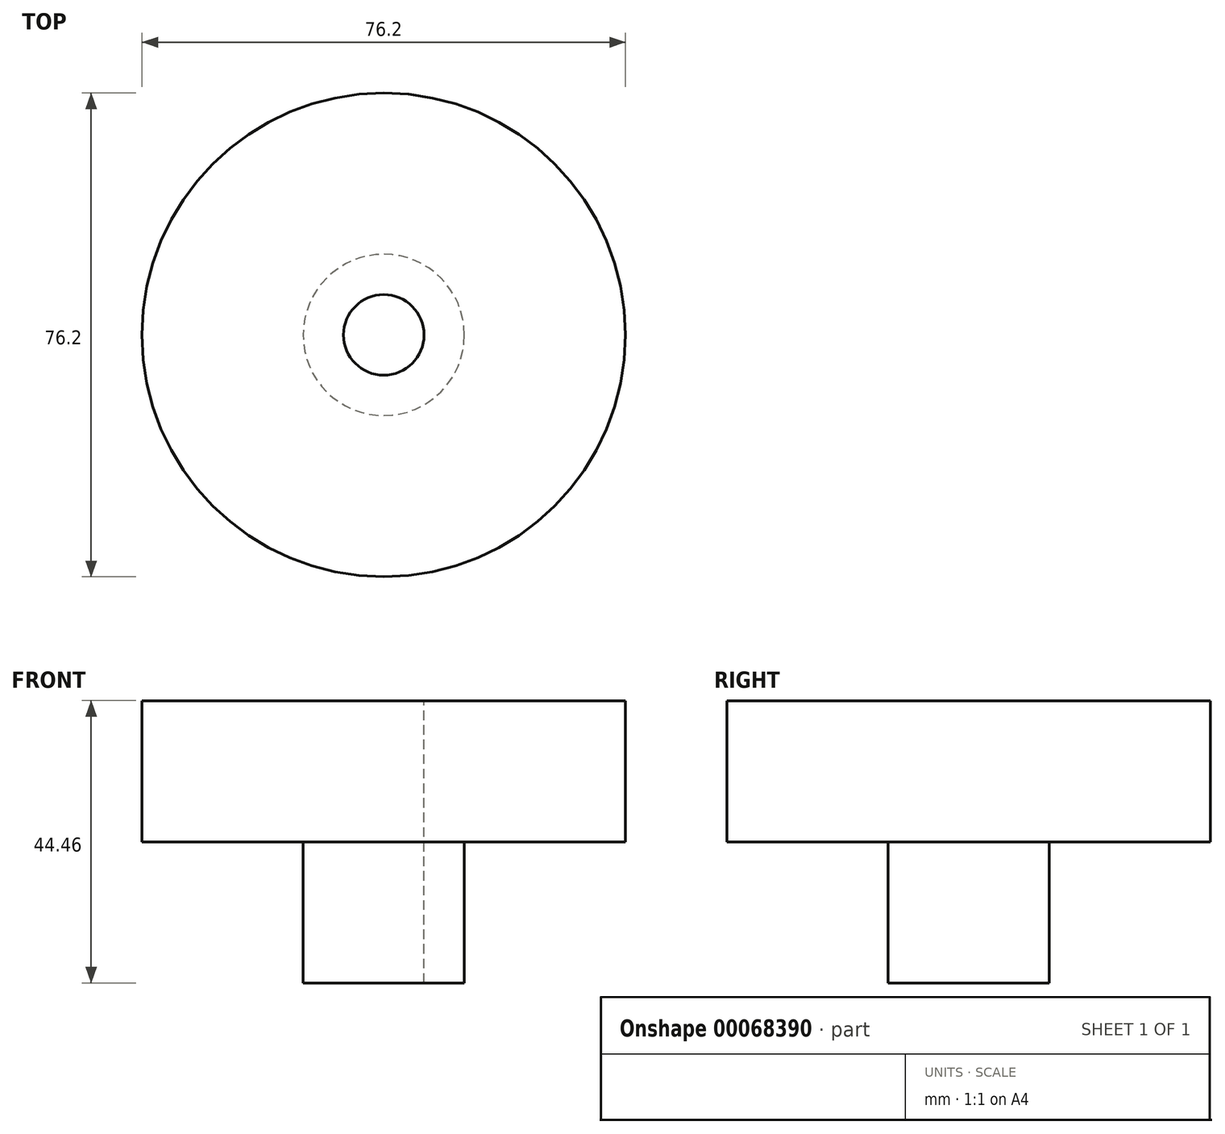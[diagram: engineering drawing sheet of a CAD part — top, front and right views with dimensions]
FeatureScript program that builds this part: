
annotation { "Feature Type Name" : "Feature", "Feature Type Description" : "" }
export const myFeature = defineFeature(function(context is Context, id is Id, definition is map)
    precondition{}
    {
        {
            var Q0;
            Q0=qCreatedBy(makeId("Top.planeOp"),FACE);
            var sketch = newSketch(context, id + "F0", { "sketchPlane" : qUnion([Q0])});
            skCircle(sketch, "E0", {"center": v(0, 0) * mm, "radius": 38.1 * mm});
            skSolve(sketch);
        }
        {
            var Q0;
            Q0=makeQuery(id+"F0.imprint","IMPRINT",FACE,{"disambiguationData":[TD([[makeQuery(id+"F0.imprint","IMPRINT",EDGE,{"derivedFrom":sQuery(id+"F0.wireOp",EDGE,"E0")}),1.0]])]});
            extrude(context, id + "F1", {"entities" : qUnion([Q0]), "depth" : 22.22 * mm});
        }
        {
            var Q0;
            Q0=makeQuery(id+"F1.opExtrude","CAP_FACE",FACE,{"disambiguationData":[OSD([sQuery(id+"F0.wireOp",EDGE,"E0")])],"isStart":false});
            var sketch = newSketch(context, id + "F2", { "sketchPlane" : qUnion([Q0])});
            skCircle(sketch, "E1", {"center": v(0, 0) * mm, "radius": 6.35 * mm});
            skSolve(sketch);
        }
        {
            var Q0;
            Q0=makeQuery(id+"F2.imprint","IMPRINT",FACE,{"disambiguationData":[TD([[makeQuery(id+"F2.imprint","IMPRINT",EDGE,{"derivedFrom":sQuery(id+"F2.wireOp",EDGE,"E1")}),1.0]])]});
            extrude(context, id + "F3", {"entities" : qUnion([Q0]), "operationType" : NewBodyOperationType.REMOVE, "oppositeDirection" : true, "depth" : 35.5 * mm});
        }
        {
            var Q0;
            Q0=makeQuery(id+"F1.opExtrude","CAP_FACE",FACE,{"disambiguationData":[OSD([sQuery(id+"F0.wireOp",EDGE,"E0")])],"isStart":true});
            var sketch = newSketch(context, id + "F4", { "sketchPlane" : qUnion([Q0])});
            skCircle(sketch, "E2", {"center": v(0, 0) * mm, "radius": 12.7 * mm});
            skSolve(sketch);
        }
        {
            var Q0;
            Q0=makeQuery(id+"F4.imprint","IMPRINT",FACE,{"disambiguationData":[TD([[makeQuery(id+"F4.imprint","IMPRINT",EDGE,{"derivedFrom":sQuery(id+"F4.wireOp",EDGE,"E2")}),1.0]])]});
            extrude(context, id + "F5", {"entities" : qUnion([Q0]), "operationType" : NewBodyOperationType.ADD, "depth" : 22.22 * mm});
        }
    });
